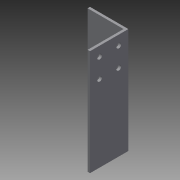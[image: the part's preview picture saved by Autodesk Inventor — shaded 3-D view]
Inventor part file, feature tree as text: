
AUTODESK INVENTOR PART (.ipt)
format: ipt  version: 2015 SP1 (Build 190203100, 203)  size: 101,888 bytes
history: native  units: in
note: dims shown in document units (in); Inventor stores cm internally (conversion verified against a paired STEP export)
features: sketch x3, hole x2, projected_geometry x2, extrude x1
ambient origin geometry x8: Origin, YZ Plane, XZ Plane, XY Plane, X Axis, Y Axis, Z Axis, Center Point
bodies: Solid1 (feature_tree)
feature tree (8):
  extrude  "Extrusion1"  Depth=2.0in
  hole  "Hole1"  [1 undecoded]
  hole  "Hole2"  [1 undecoded]
  sketch  "Sketch1"  dims[d0=0.125in d1=2.0in]
  sketch  "Sketch2"  dims[d2=2.0in d3=0.125in]
  projected_geometry  "Projected Loop1"
  sketch  "Sketch3"  dims[d4=5.25in d5=0.0in d6=0.5in d7=0.5in d8=0.5in d9=0.5in d10=0.5in d11=0.5in d12=1.5in d13=1.5in d14=0.25in d15=0.75in d16=0.375in d17=0.25in d18=0.5635in d19=1.0in d20=0.8108in d21=0.5in d22=0.5in d23=2.5in d24=2.5in d25=0.25in d26=0.75in d27=0.375in d28=0.25in d29=0.5635in d30=1.0in d31=0.8108in]
  projected_geometry  "Projected Loop2"
note: 2 required parameter values undecoded (feature->parameter linkage not recoverable at this tier; creation-order binding heuristic only, values carry confidence <= 0.55)
